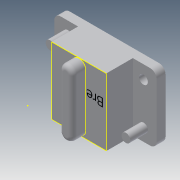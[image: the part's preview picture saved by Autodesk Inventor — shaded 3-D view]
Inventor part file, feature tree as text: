
AUTODESK INVENTOR PART (.ipt)
format: ipt  version: 2014 (Build 180170000, 170)  size: 151,040 bytes
history: native  units: in
note: dims shown in document units (in); Inventor stores cm internally (conversion verified against a paired STEP export)
features: sketch x5, extrude x4, fillet x1, projected_geometry x1
ambient origin geometry x8: Origin, YZ Plane, XZ Plane, XY Plane, X Axis, Y Axis, Z Axis, Center Point
bodies: Solid1 (feature_tree)
feature tree (11):
  extrude  "Extrusion1"  Depth=1.9in
  extrude  "Extrusion2"  Depth=0.25in
  extrude  "Extrusion3"  Depth=0.25in TaperAngle=0.0deg
  fillet  "Fillet1"  Radius=1.55in
  extrude  "Extrusion4"  Depth=0.375in TaperAngle=0.0deg
  sketch  "Sketch5"  dims[d12=0.125in d13=0.5in d14=0.0in d15=0.375in d16=0.375in d17=0.375in d18=0.375in]
  sketch  "Sketch1"  dims[d0=2.9in d1=1.9in]
  sketch  "Sketch2"  dims[d2=0.1875in d3=0.25in]
  sketch  "Sketch3"  dims[d4=0.25in d5=0.25in d6=0.0in d7=1.55in]
  sketch  "Sketch4"  dims[d8=0.75in d9=0.0in d10=0.375in d11=0.0in]
  projected_geometry  "Projected Loop1"
